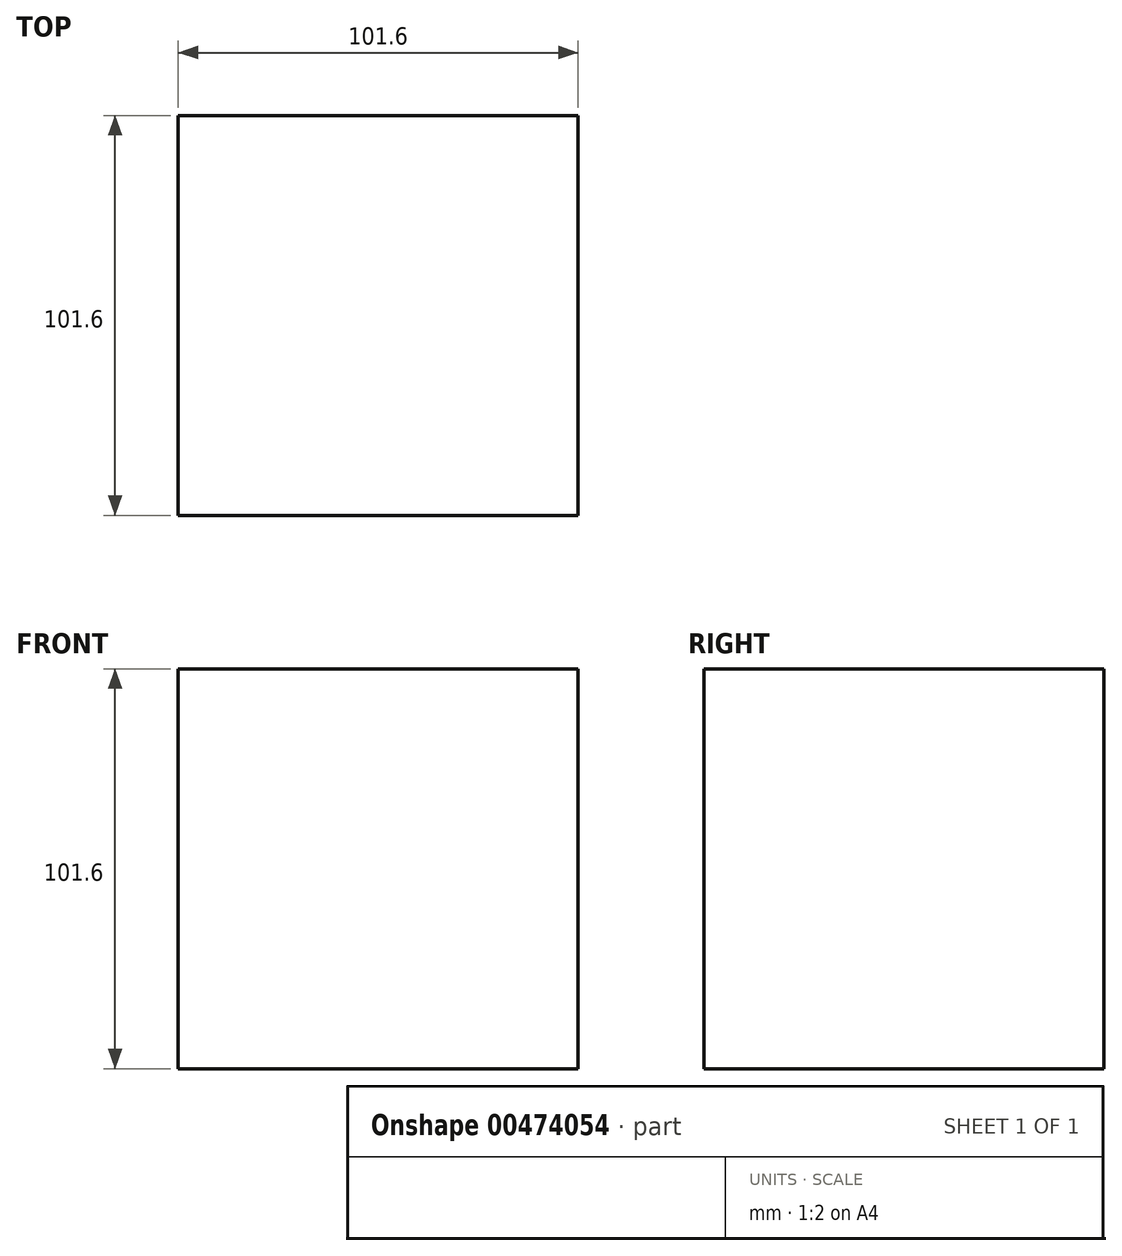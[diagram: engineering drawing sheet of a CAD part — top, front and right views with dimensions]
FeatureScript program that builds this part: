
annotation { "Feature Type Name" : "Feature", "Feature Type Description" : "" }
export const myFeature = defineFeature(function(context is Context, id is Id, definition is map)
    precondition{}
    {
        {
            var Q0;
            Q0=qCreatedBy(makeId("Front.planeOp"),FACE);
            var sketch = newSketch(context, id + "F0", { "sketchPlane" : qUnion([Q0])});
            skLineSegment(sketch, "E0.bottom", {"start": v(50.8, -50.8) * mm, "end": v(-50.8, -50.8) * mm});
            skLineSegment(sketch, "E0.top", {"start": v(50.8, 50.8) * mm, "end": v(-50.8, 50.8) * mm});
            skLineSegment(sketch, "E0.left", {"start": v(50.8, -50.8) * mm, "end": v(50.8, 50.8) * mm});
            skLineSegment(sketch, "E0.right", {"start": v(-50.8, -50.8) * mm, "end": v(-50.8, 50.8) * mm});
            skPoint(sketch, "E0.middle", {"position": v(0, 0) * mm});
            skSolve(sketch);
        }
        {
            var Q0;
            Q0=makeQuery(id+"F0.imprint","IMPRINT",FACE,{"disambiguationData":[TD([[makeQuery(id+"F0.imprint","IMPRINT",EDGE,{"derivedFrom":sQuery(id+"F0.wireOp",EDGE,"E0.bottom")}),-1.0]])]});
            extrude(context, id + "F1", {"entities" : qUnion([Q0]), "endBound" : BoundingType.SYMMETRIC, "depth" : 101.6 * mm});
        }
    });
